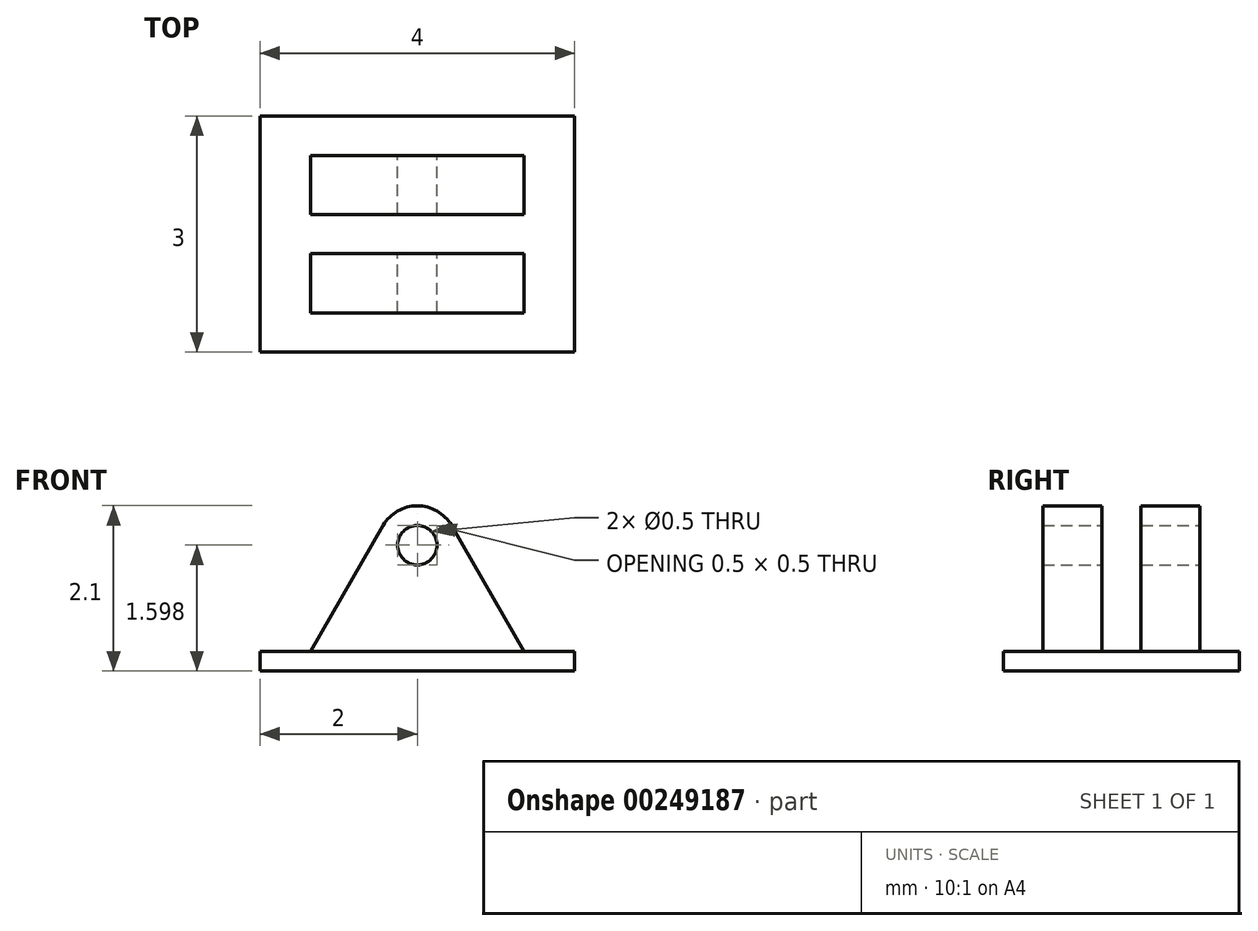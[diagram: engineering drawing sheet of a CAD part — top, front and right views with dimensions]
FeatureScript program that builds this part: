
annotation { "Feature Type Name" : "Feature", "Feature Type Description" : "" }
export const myFeature = defineFeature(function(context is Context, id is Id, definition is map)
    precondition{}
    {
        {
            var Q0;
            Q0=qCreatedBy(makeId("Top.planeOp"),FACE);
            var sketch = newSketch(context, id + "F0", { "sketchPlane" : qUnion([Q0])});
            skLineSegment(sketch, "E0.bottom", {"start": v(-2, 1.5) * mm, "end": v(2, 1.5) * mm});
            skLineSegment(sketch, "E0.top", {"start": v(-2, -1.5) * mm, "end": v(2, -1.5) * mm});
            skLineSegment(sketch, "E0.left", {"start": v(-2, 1.5) * mm, "end": v(-2, -1.5) * mm});
            skLineSegment(sketch, "E0.right", {"start": v(2, 1.5) * mm, "end": v(2, -1.5) * mm});
            skPoint(sketch, "E0.middle", {"position": v(0, 0) * mm});
            skSolve(sketch);
        }
        {
            var Q0;
            Q0=makeQuery(id+"F0.imprint","IMPRINT",FACE,{"disambiguationData":[TD([[makeQuery(id+"F0.imprint","IMPRINT",EDGE,{"derivedFrom":sQuery(id+"F0.wireOp",EDGE,"E0.bottom")}),-1.0]])]});
            extrude(context, id + "F1", {"entities" : qUnion([Q0]), "depth" : .25 * mm});
        }
        {
            var Q0;
            Q0=qCreatedBy(makeId("Front.planeOp"),FACE);
            var sketch = newSketch(context, id + "F2", { "sketchPlane" : qUnion([Q0])});
            skLineSegment(sketch, "E1.0.0", {"start": v(-2, 0) * mm, "end": v(2, 0) * mm});
            skLineSegment(sketch, "E1.0.1", {"start": v(2, 0) * mm, "end": v(2, 0.25) * mm});
            skLineSegment(sketch, "E1.0.2", {"start": v(2, 0.25) * mm, "end": v(-2, 0.25) * mm});
            skLineSegment(sketch, "E1.0.3", {"start": v(-2, 0.25) * mm, "end": v(-2, 0) * mm});
            skLineSegment(sketch, "E2", {"start": v(-1.5, 0) * mm, "end": v(-0.43, 1.85) * mm});
            skLineSegment(sketch, "E3", {"start": v(0.43, 1.85) * mm, "end": v(1.5, 0) * mm});
            skArc(sketch, "E4", {"start": v(0.43, 1.85) * mm, "mid": v(0, 2.1) * mm, "end": v(-0.43, 1.85) * mm});
            skPoint(sketch, "E5.orphan", {"position": v(0, 2.6) * mm});
            skCircle(sketch, "E6", {"center": v(0, 1.6) * mm, "radius": 0.25 * mm});
            skSolve(sketch);
        }
        {
            var Q0;
            {var subQ0=sQuery(id+"F2.wireOp",EDGE,"E4");Q0=makeQuery(id+"F2.imprint","IMPRINT",FACE,{"disambiguationData":[TD([[makeQuery(id+"F2.imprint","IMPRINT",EDGE,{"derivedFrom":subQ0}),1.0]])]});}
            extrude(context, id + "F3", {"entities" : qUnion([Q0]), "operationType" : NewBodyOperationType.ADD, "endBound" : BoundingType.SYMMETRIC, "depth" : 2 * mm});
        }
        {
            var Q0;
            Q0=qCreatedBy(makeId("Right.planeOp"),FACE);
            var sketch = newSketch(context, id + "F4", { "sketchPlane" : qUnion([Q0])});
            skLineSegment(sketch, "E7.0.1", {"start": v(-1.5, 0) * mm, "end": v(-1.5, 0.25) * mm});
            skLineSegment(sketch, "E7.0.2", {"start": v(-1.5, 0.25) * mm, "end": v(0.25, 0.25) * mm});
            skLineSegment(sketch, "E7.0.3", {"start": v(1.5, 0.25) * mm, "end": v(1.5, 0) * mm});
            skLineSegment(sketch, "E8.0.0", {"start": v(1, 1.85) * mm, "end": v(1, 0.25) * mm});
            skLineSegment(sketch, "E8.0.1", {"start": v(0.25, 0.25) * mm, "end": v(-0.25, 0.25) * mm});
            skLineSegment(sketch, "E9.top", {"start": v(0.25, 4.4) * mm, "end": v(-0.25, 4.4) * mm});
            skLineSegment(sketch, "E9.left", {"start": v(0.25, 0.25) * mm, "end": v(0.25, 4.4) * mm});
            skLineSegment(sketch, "E9.right", {"start": v(-0.25, 0.25) * mm, "end": v(-0.25, 4.4) * mm});
            skPoint(sketch, "E9.middle", {"position": v(0, 2.32) * mm});
            skPoint(sketch, "E10.orphan", {"position": v(-1, 1.85) * mm});
            skPoint(sketch, "E11.orphan", {"position": v(-1, 0.25) * mm});
            skSolve(sketch);
        }
        {
            var Q0;
            Q0=makeQuery(id+"F4.imprint","IMPRINT",FACE,{"disambiguationData":[TD([[makeQuery(id+"F4.imprint","IMPRINT",EDGE,{"derivedFrom":sQuery(id+"F4.wireOp",EDGE,"E9.top")}),1.0]])]});
            extrude(context, id + "F5", {"entities" : qUnion([Q0]), "operationType" : NewBodyOperationType.REMOVE, "endBound" : BoundingType.SYMMETRIC, "oppositeDirection" : true, "depth" : 25 * mm});
        }
    });
